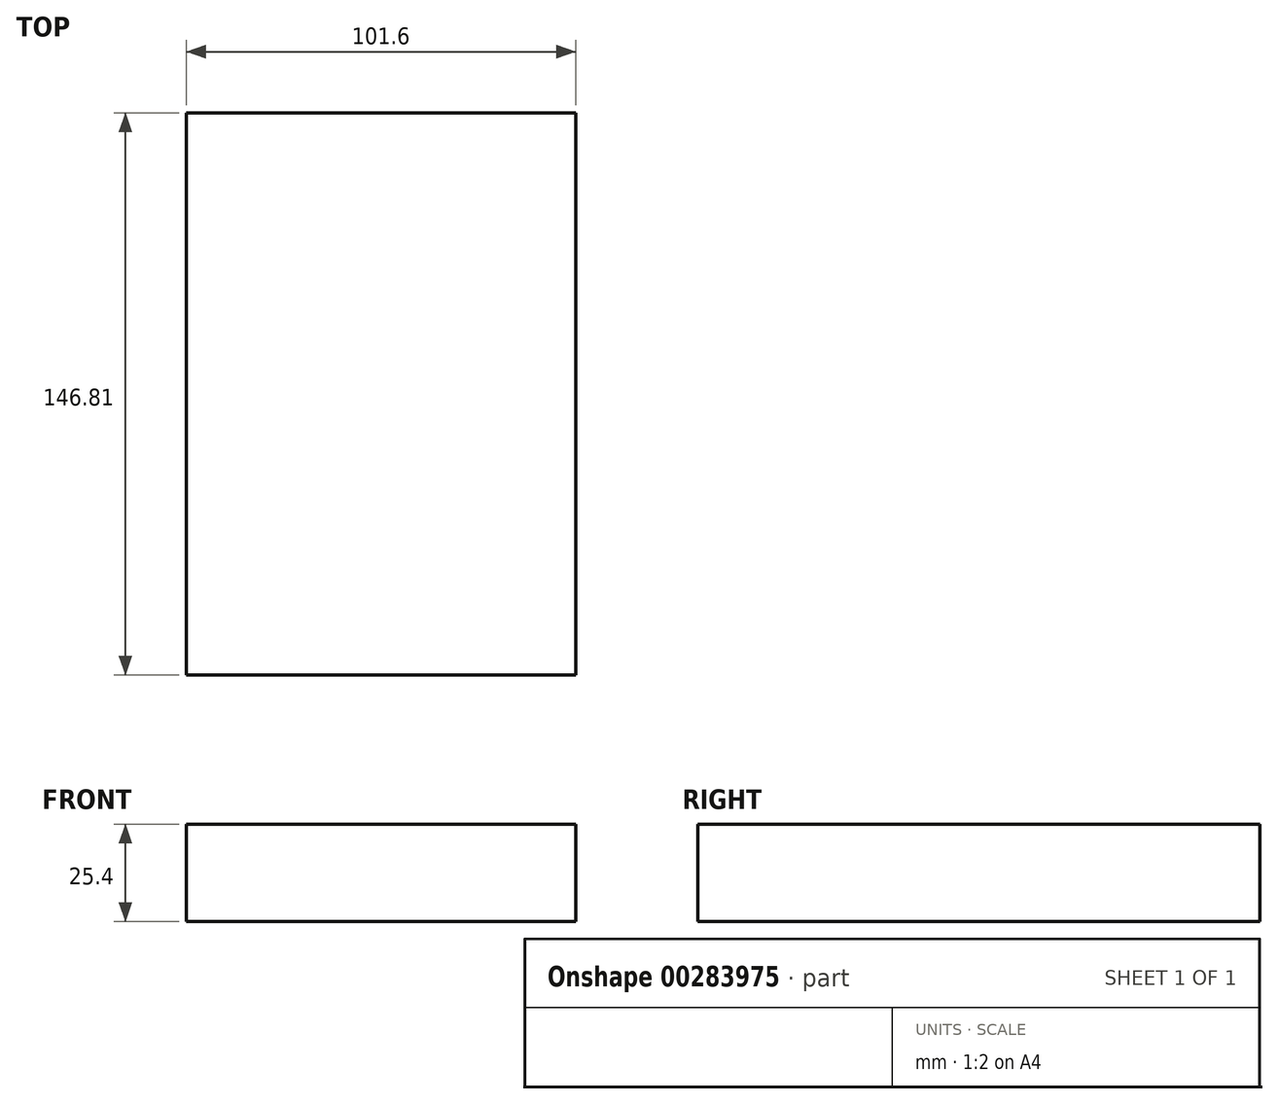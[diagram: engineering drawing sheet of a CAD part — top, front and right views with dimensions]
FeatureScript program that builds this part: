
annotation { "Feature Type Name" : "Feature", "Feature Type Description" : "" }
export const myFeature = defineFeature(function(context is Context, id is Id, definition is map)
    precondition{}
    {
        {
            var Q0;
            Q0=qCreatedBy(makeId("Top.planeOp"),FACE);
            var sketch = newSketch(context, id + "F0", { "sketchPlane" : qUnion([Q0])});
            skLineSegment(sketch, "E0.bottom", {"start": v(0, 0) * mm, "end": v(101.6, 0) * mm});
            skLineSegment(sketch, "E0.top", {"start": v(0, 146.81) * mm, "end": v(101.6, 146.81) * mm});
            skLineSegment(sketch, "E0.left", {"start": v(0, 0) * mm, "end": v(0, 146.81) * mm});
            skLineSegment(sketch, "E0.right", {"start": v(101.6, 0) * mm, "end": v(101.6, 146.81) * mm});
            skSolve(sketch);
        }
        {
            var Q0;
            Q0=makeQuery(id+"F0.imprint","IMPRINT",FACE,{"disambiguationData":[TD([[makeQuery(id+"F0.imprint","IMPRINT",EDGE,{"derivedFrom":sQuery(id+"F0.wireOp",EDGE,"E0.bottom")}),1.0]])]});
            extrude(context, id + "F1", {"entities" : qUnion([Q0]), "depth" : 25.4 * mm});
        }
    });
